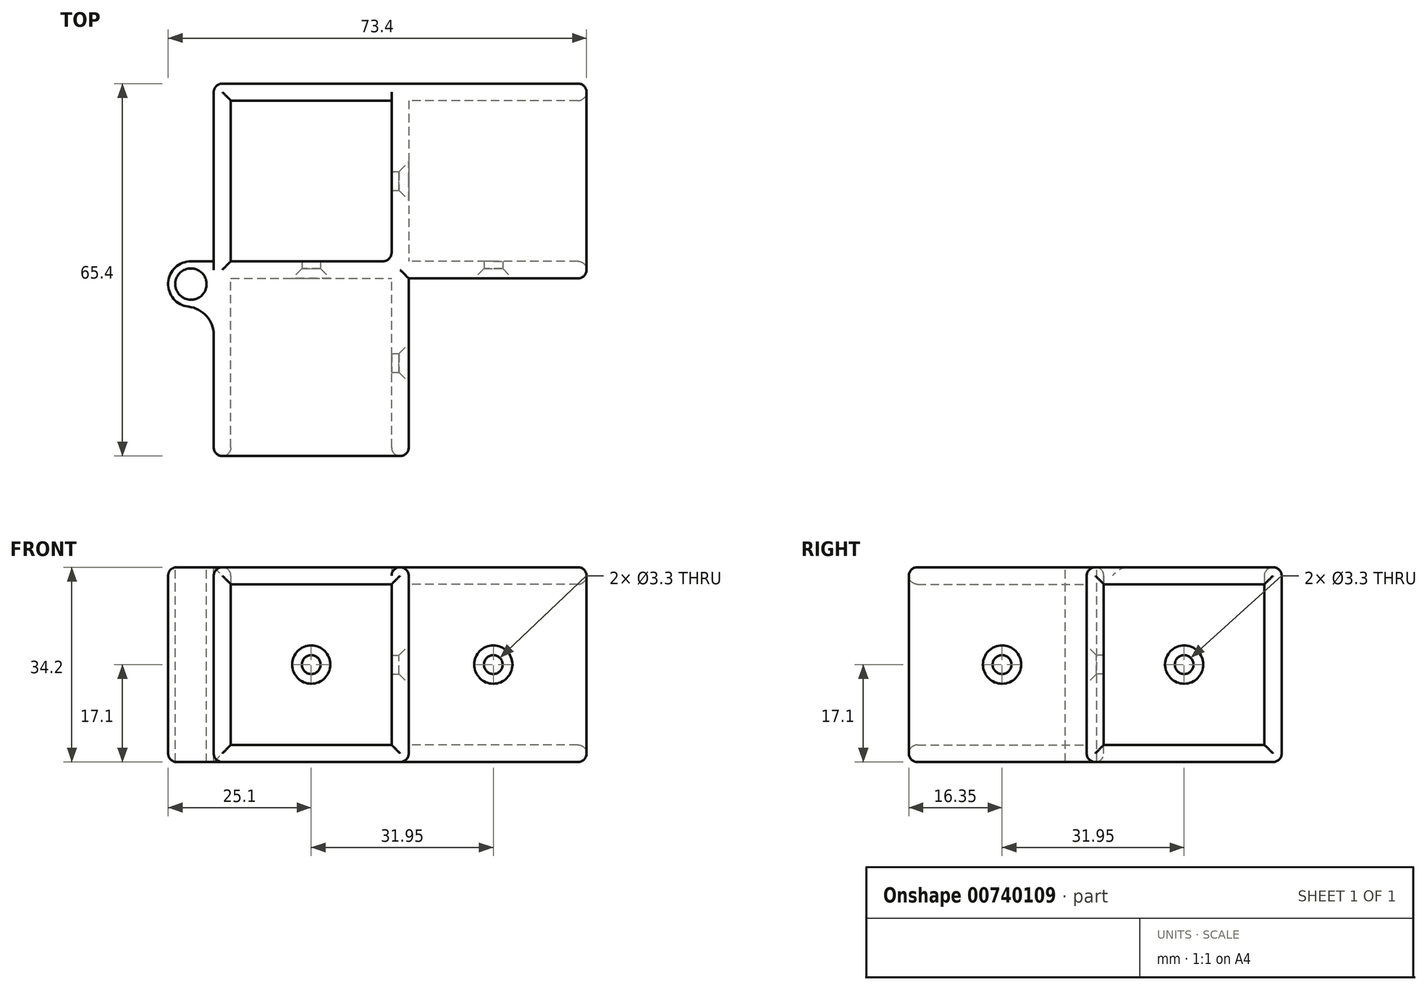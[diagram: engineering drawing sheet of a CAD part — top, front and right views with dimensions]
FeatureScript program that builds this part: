
annotation { "Feature Type Name" : "Feature", "Feature Type Description" : "" }
export const myFeature = defineFeature(function(context is Context, id is Id, definition is map)
    precondition{}
    {
        {
            var Q0;
            Q0=qCreatedBy(makeId("Top.planeOp"),FACE);
            var sketch = newSketch(context, id + "F0", { "sketchPlane" : qUnion([Q0])});
            skLineSegment(sketch, "E0.bottom", {"start": v(0, 0) * mm, "end": v(-28.2, 0) * mm});
            skLineSegment(sketch, "E0.top", {"start": v(0, 28.2) * mm, "end": v(-28.2, 28.2) * mm});
            skLineSegment(sketch, "E0.left", {"start": v(0, 0) * mm, "end": v(0, 28.2) * mm});
            skLineSegment(sketch, "E0.right", {"start": v(-28.2, 0) * mm, "end": v(-28.2, 28.2) * mm});
            skLineSegment(sketch, "E1.0", {"start": v(3, 31.2) * mm, "end": v(-31.2, 31.2) * mm});
            skLineSegment(sketch, "E1.1", {"start": v(3, -3) * mm, "end": v(3, 31.2) * mm});
            skLineSegment(sketch, "E1.2", {"start": v(3, -3) * mm, "end": v(-31.2, -3) * mm});
            skLineSegment(sketch, "E1.3", {"start": v(-31.2, -3) * mm, "end": v(-31.2, 31.2) * mm});
            skPoint(sketch, "E2", {"position": v(-14.1, 14.1) * mm});
            skSolve(sketch);
        }
        {
            var Q0;
            Q0=makeQuery(id+"F0.imprint","IMPRINT",FACE,{"disambiguationData":[TD([[makeQuery(id+"F0.imprint","IMPRINT",EDGE,{"derivedFrom":sQuery(id+"F0.wireOp",EDGE,"E0.bottom")}),1.0]])]});
            var Q1;
            Q1=makeQuery(id+"F0.imprint","IMPRINT",FACE,{"disambiguationData":[TD([[makeQuery(id+"F0.imprint","IMPRINT",EDGE,{"derivedFrom":sQuery(id+"F0.wireOp",EDGE,"E0.bottom")}),-1.0]])]});
            extrude(context, id + "F1", {"entities" : qUnion([Q0, Q1]), "oppositeDirection" : true, "depth" : 3 * mm, "offsetDistance" : 25 * mm});
        }
        {
            var Q0;
            Q0=makeQuery(id+"F0.imprint","IMPRINT",FACE,{"disambiguationData":[TD([[makeQuery(id+"F0.imprint","IMPRINT",EDGE,{"derivedFrom":sQuery(id+"F0.wireOp",EDGE,"E0.bottom")}),1.0]])]});
            extrude(context, id + "F2", {"entities" : qUnion([Q0]), "operationType" : NewBodyOperationType.ADD, "depth" : 31.2 * mm, "offsetDistance" : 25 * mm});
        }
        {
            var Q0;
            {var subQ0=sQuery(id+"F0.wireOp",EDGE,"E1.2");Q0=makeQuery(id+"F2.boolean.opBoolean","MERGE",FACE,{"derivedFrom":[makeQuery(id+"F1.opExtrude","SWEPT_FACE",FACE,{"disambiguationData":[OSD([subQ0])]}),makeQuery(id+"F2.opExtrude","SWEPT_FACE",FACE,{"disambiguationData":[OSD([subQ0])]})]});}
            var sketch = newSketch(context, id + "F3", { "sketchPlane" : qUnion([Q0])});
            skLineSegment(sketch, "E3.bottom", {"start": v(-31.2, 31.2) * mm, "end": v(3, 31.2) * mm});
            skLineSegment(sketch, "E3.top", {"start": v(-31.2, -3) * mm, "end": v(3, -3) * mm});
            skLineSegment(sketch, "E3.left", {"start": v(-31.2, 31.2) * mm, "end": v(-31.2, -3) * mm});
            skLineSegment(sketch, "E3.right", {"start": v(3, 31.2) * mm, "end": v(3, -3) * mm});
            skLineSegment(sketch, "E4.0", {"start": v(-28.2, 28.2) * mm, "end": v(0, 28.2) * mm});
            skLineSegment(sketch, "E4.1", {"start": v(-28.2, 28.2) * mm, "end": v(-28.2, 0) * mm});
            skLineSegment(sketch, "E4.2", {"start": v(-28.2, 0) * mm, "end": v(0, 0) * mm});
            skLineSegment(sketch, "E4.3", {"start": v(0, 28.2) * mm, "end": v(0, 0) * mm});
            skPoint(sketch, "E5", {"position": v(-14.1, 14.1) * mm});
            skSolve(sketch);
        }
        {
            var Q0;
            Q0=makeQuery(id+"F3.imprint","IMPRINT",FACE,{"disambiguationData":[TD([[makeQuery(id+"F3.imprint","IMPRINT",EDGE,{"derivedFrom":sQuery(id+"F3.wireOp",EDGE,"E3.bottom")}),1.0]])]});
            extrude(context, id + "F4", {"entities" : qUnion([Q0]), "operationType" : NewBodyOperationType.ADD, "depth" : 31.2 * mm, "offsetDistance" : 25 * mm});
        }
        {
            var Q0;
            {var subQ0=sQuery(id+"F0.wireOp",EDGE,"E1.1");Q0=makeQuery(id+"F4.boolean.opBoolean","MERGE",FACE,{"derivedFrom":[makeQuery(id+"F2.boolean.opBoolean","MERGE",FACE,{"derivedFrom":[makeQuery(id+"F1.opExtrude","SWEPT_FACE",FACE,{"disambiguationData":[OSD([subQ0])]}),makeQuery(id+"F2.opExtrude","SWEPT_FACE",FACE,{"disambiguationData":[OSD([subQ0])]})]}),makeQuery(id+"F4.opExtrude","SWEPT_FACE",FACE,{"disambiguationData":[OSD([sQuery(id+"F3.wireOp",EDGE,"E3.right")])]})]});}
            var sketch = newSketch(context, id + "F5", { "sketchPlane" : qUnion([Q0])});
            skLineSegment(sketch, "E6.bottom", {"start": v(31.2, 31.2) * mm, "end": v(-3, 31.2) * mm});
            skLineSegment(sketch, "E6.top", {"start": v(31.2, -3) * mm, "end": v(-3, -3) * mm});
            skLineSegment(sketch, "E6.left", {"start": v(31.2, 31.2) * mm, "end": v(31.2, -3) * mm});
            skLineSegment(sketch, "E6.right", {"start": v(-3, 31.2) * mm, "end": v(-3, -3) * mm});
            skLineSegment(sketch, "E7.0", {"start": v(28.2, 28.2) * mm, "end": v(0, 28.2) * mm});
            skLineSegment(sketch, "E7.1", {"start": v(28.2, 28.2) * mm, "end": v(28.2, 0) * mm});
            skLineSegment(sketch, "E7.2", {"start": v(28.2, 0) * mm, "end": v(0, 0) * mm});
            skLineSegment(sketch, "E7.3", {"start": v(0, 28.2) * mm, "end": v(0, 0) * mm});
            skPoint(sketch, "E8", {"position": v(14.1, 14.1) * mm});
            skSolve(sketch);
        }
        {
            var Q0;
            Q0=qSketchRegion(id+"F5",true);
            extrude(context, id + "F6", {"entities" : qUnion([Q0]), "operationType" : NewBodyOperationType.ADD, "depth" : 31.2 * mm, "offsetDistance" : 25 * mm});
        }
        {
            var Q0;
            Q0=sQuery(id+"F5.wireOp",VERTEX,"E8");
            var Q1;
            Q1=sQuery(id+"F3.wireOp",VERTEX,"E5");
            var Q2;
            Q2=makeQuery(id+"F1.opExtrude","SWEPT_BODY",BODY,{"disambiguationData":[OSD([sQuery(id+"F0.wireOp",EDGE,"E1.0"),sQuery(id+"F0.wireOp",EDGE,"E1.1"),sQuery(id+"F0.wireOp",EDGE,"E1.2"),sQuery(id+"F0.wireOp",EDGE,"E1.3")])]});
            hole(context, id + "F7", {"style" : HoleStyle.C_SINK, "endStyle" : HoleEndStyle.BLIND, "standardTappedOrClearance" : lookupTablePath({ "standard" : "ISO", "fit" : "Normal", "size" : "M3", "type" : "Clearance" }), "standardBlindInLast" : lookupTablePath({ "fit" : "Standard", "standard" : "ISO", "size" : "M3", "type" : "Clearance" }), "holeDiameter" : 3.3 * mm, "cSinkDiameter" : 6.72 * mm, "cSinkAngle" : 90 * degree, "majorDiameter" : 5 * mm, "holeDepth" : 13.5 * mm, "isTappedThrough" : true, "tappedDepth" : 12 * mm, "tapClearance" : 3, "startFromSketch" : true, "locations" : qUnion([Q0, Q1]), "scope" : qUnion([Q2])});
        }
        {
            var Q0;
            {var subQ0=sQuery(id+"F3.wireOp",EDGE,"E3.bottom");var subQ3=sQuery(id+"F0.wireOp",EDGE,"E1.1");var subQ5=sQuery(id+"F3.wireOp",EDGE,"E3.right");Q0=makeQuery(id+"F6.boolean.opBoolean","SPLIT",FACE,{"disambiguationData":[TD([makeQuery(id+"F4.opExtrude","SWEPT_FACE",FACE,{"disambiguationData":[OSD([subQ0])]})])],"derivedFrom":makeQuery(id+"F4.boolean.opBoolean","MERGE",FACE,{"derivedFrom":[makeQuery(id+"F2.boolean.opBoolean","MERGE",FACE,{"derivedFrom":[makeQuery(id+"F1.opExtrude","SWEPT_FACE",FACE,{"disambiguationData":[OSD([subQ3])]}),makeQuery(id+"F2.opExtrude","SWEPT_FACE",FACE,{"disambiguationData":[OSD([subQ3])]})]}),makeQuery(id+"F4.opExtrude","SWEPT_FACE",FACE,{"disambiguationData":[OSD([subQ5])]})]})});}
            var sketch = newSketch(context, id + "F8", { "sketchPlane" : qUnion([Q0])});
            skPoint(sketch, "E9", {"position": v(-17.85, 14.1) * mm});
            skSolve(sketch);
        }
        {
            var Q0;
            Q0=makeQuery(id+"F6.opExtrude","SWEPT_FACE",FACE,{"disambiguationData":[OSD([sQuery(id+"F5.wireOp",EDGE,"E6.right")])]});
            var sketch = newSketch(context, id + "F9", { "sketchPlane" : qUnion([Q0])});
            skPoint(sketch, "E10", {"position": v(17.85, 14.1) * mm});
            skSolve(sketch);
        }
        {
            var Q0;
            Q0=sQuery(id+"F9.wireOp",VERTEX,"E10");
            var Q1;
            Q1=sQuery(id+"F8.wireOp",VERTEX,"E9");
            var Q2;
            Q2=makeQuery(id+"F1.opExtrude","SWEPT_BODY",BODY,{"disambiguationData":[OSD([sQuery(id+"F0.wireOp",EDGE,"E1.0"),sQuery(id+"F0.wireOp",EDGE,"E1.1"),sQuery(id+"F0.wireOp",EDGE,"E1.2"),sQuery(id+"F0.wireOp",EDGE,"E1.3")])]});
            hole(context, id + "F10", {"style" : HoleStyle.C_SINK, "endStyle" : HoleEndStyle.BLIND, "standardTappedOrClearance" : lookupTablePath({ "standard" : "ISO", "fit" : "Normal", "size" : "M3", "type" : "Clearance" }), "standardBlindInLast" : lookupTablePath({ "fit" : "Standard", "standard" : "ISO", "size" : "M3", "type" : "Clearance" }), "holeDiameter" : 3.3 * mm, "cSinkDiameter" : 6.72 * mm, "cSinkAngle" : 90 * degree, "majorDiameter" : 5 * mm, "holeDepth" : 13.5 * mm, "isTappedThrough" : true, "tappedDepth" : 12 * mm, "tapClearance" : 3, "startFromSketch" : true, "locations" : qUnion([Q0, Q1]), "scope" : qUnion([Q2])});
        }
        {
            var Q0;
            Q0=makeQuery(id+"F6.boolean.opBoolean","MERGE",FACE,{"derivedFrom":[makeQuery(id+"F4.boolean.opBoolean","MERGE",FACE,{"derivedFrom":[makeQuery(id+"F2.opExtrude","CAP_FACE",FACE,{"disambiguationData":[OSD([sQuery(id+"F0.wireOp",EDGE,"E0.bottom"),sQuery(id+"F0.wireOp",EDGE,"E0.top"),sQuery(id+"F0.wireOp",EDGE,"E0.left"),sQuery(id+"F0.wireOp",EDGE,"E0.right"),sQuery(id+"F0.wireOp",EDGE,"E1.0"),sQuery(id+"F0.wireOp",EDGE,"E1.1"),sQuery(id+"F0.wireOp",EDGE,"E1.2"),sQuery(id+"F0.wireOp",EDGE,"E1.3")])],"isStart":false}),makeQuery(id+"F4.opExtrude","SWEPT_FACE",FACE,{"disambiguationData":[OSD([sQuery(id+"F3.wireOp",EDGE,"E3.bottom")])]})]}),makeQuery(id+"F6.opExtrude","SWEPT_FACE",FACE,{"disambiguationData":[OSD([sQuery(id+"F5.wireOp",EDGE,"E6.bottom")])]})]});
            var sketch = newSketch(context, id + "F11", { "sketchPlane" : qUnion([Q0])});
            skArc(sketch, "E11", {"start": v(-35.2, 0) * mm, "mid": v(-39.2, -4) * mm, "end": v(-35.2, -8) * mm});
            skLineSegment(sketch, "E12", {"start": v(-31.2, 0) * mm, "end": v(-35.2, 0) * mm});
            skLineSegment(sketch, "E13", {"start": v(-31.2, -8) * mm, "end": v(-35.2, -8) * mm});
            skSolve(sketch);
        }
        {
            var Q0;
            Q0=makeQuery(id+"F11.imprint","IMPRINT",FACE,{"disambiguationData":[TD([[makeQuery(id+"F11.imprint","IMPRINT",EDGE,{"derivedFrom":sQuery(id+"F11.wireOp",EDGE,"E11")}),1.0]])]});
            var Q1;
            Q1=makeQuery(id+"F6.boolean.opBoolean","MERGE",FACE,{"derivedFrom":[makeQuery(id+"F4.boolean.opBoolean","MERGE",FACE,{"derivedFrom":[makeQuery(id+"F1.opExtrude","CAP_FACE",FACE,{"disambiguationData":[OSD([sQuery(id+"F0.wireOp",EDGE,"E1.0"),sQuery(id+"F0.wireOp",EDGE,"E1.1"),sQuery(id+"F0.wireOp",EDGE,"E1.2"),sQuery(id+"F0.wireOp",EDGE,"E1.3")])],"isStart":false}),makeQuery(id+"F4.opExtrude","SWEPT_FACE",FACE,{"disambiguationData":[OSD([sQuery(id+"F3.wireOp",EDGE,"E3.top")])]})]}),makeQuery(id+"F6.opExtrude","SWEPT_FACE",FACE,{"disambiguationData":[OSD([sQuery(id+"F5.wireOp",EDGE,"E6.top")])]})]});
            extrude(context, id + "F12", {"entities" : qUnion([Q0]), "operationType" : NewBodyOperationType.ADD, "endBound" : BoundingType.UP_TO_SURFACE, "oppositeDirection" : true, "depth" : 25 * mm, "endBoundEntityFace" : qUnion([Q1]), "offsetDistance" : 25 * mm});
        }
        {
            var Q0;
            Q0=makeQuery(id+"F12.opExtrude","SWEPT_EDGE",EDGE,{"disambiguationData":[OSD([sQuery(id+"F0.wireOp",EDGE,"E1.3"),sQuery(id+"F3.wireOp",EDGE,"E3.bottom"),sQuery(id+"F3.wireOp",EDGE,"E3.left"),sQuery(id+"F11.wireOp",EDGE,"E12")])]});
            var Q1;
            Q1=makeQuery(id+"F12.opExtrude","SWEPT_EDGE",EDGE,{"disambiguationData":[OSD([sQuery(id+"F0.wireOp",EDGE,"E1.3"),sQuery(id+"F3.wireOp",EDGE,"E3.bottom"),sQuery(id+"F3.wireOp",EDGE,"E3.left"),sQuery(id+"F11.wireOp",EDGE,"E13")])]});
            fillet(context, id + "F13", {"entities" : qUnion([Q0, Q1]), "radius" : 5 * mm, "tangentPropagation" : true, "allowEdgeOverflow" : false});
        }
        {
            var Q0;
            {var subQ0=sQuery(id+"F5.wireOp",EDGE,"E6.top");var subQ1=sQuery(id+"F3.wireOp",EDGE,"E3.top");var subQ2=sQuery(id+"F0.wireOp",EDGE,"E1.3");var subQ3=sQuery(id+"F0.wireOp",EDGE,"E1.2");var subQ4=sQuery(id+"F0.wireOp",EDGE,"E1.1");var subQ5=sQuery(id+"F0.wireOp",EDGE,"E1.0");Q0=makeQuery(id+"F13.opFillet","BLEND_EDGE",EDGE,{"blendedFrom":[makeQuery(id+"F12.opExtrude","SWEPT_EDGE",EDGE,{"disambiguationData":[OSD([subQ2,sQuery(id+"F3.wireOp",EDGE,"E3.bottom"),sQuery(id+"F3.wireOp",EDGE,"E3.left"),sQuery(id+"F11.wireOp",EDGE,"E13")])]}),makeQuery(id+"F12.boolean.opBoolean","MERGE",FACE,{"derivedFrom":[makeQuery(id+"F6.boolean.opBoolean","MERGE",FACE,{"derivedFrom":[makeQuery(id+"F4.boolean.opBoolean","MERGE",FACE,{"derivedFrom":[makeQuery(id+"F1.opExtrude","CAP_FACE",FACE,{"disambiguationData":[OSD([subQ5,subQ4,subQ3,subQ2])],"isStart":false}),makeQuery(id+"F4.opExtrude","SWEPT_FACE",FACE,{"disambiguationData":[OSD([subQ1])]})]}),makeQuery(id+"F6.opExtrude","SWEPT_FACE",FACE,{"disambiguationData":[OSD([subQ0])]})]}),makeQuery(id+"F12.opExtrude","CAP_FACE",FACE,{"disambiguationData":[OSD([subQ5,subQ4,subQ3,subQ2,subQ1,subQ0])],"isStart":false})]})],"blendedInto":[makeQuery(id+"F12.boolean.opBoolean","MERGE",FACE,{"derivedFrom":[makeQuery(id+"F6.boolean.opBoolean","MERGE",FACE,{"derivedFrom":[makeQuery(id+"F4.boolean.opBoolean","MERGE",FACE,{"derivedFrom":[makeQuery(id+"F1.opExtrude","CAP_FACE",FACE,{"disambiguationData":[OSD([subQ5,subQ4,subQ3,subQ2])],"isStart":false}),makeQuery(id+"F4.opExtrude","SWEPT_FACE",FACE,{"disambiguationData":[OSD([subQ1])]})]}),makeQuery(id+"F6.opExtrude","SWEPT_FACE",FACE,{"disambiguationData":[OSD([subQ0])]})]}),makeQuery(id+"F12.opExtrude","CAP_FACE",FACE,{"disambiguationData":[OSD([subQ5,subQ4,subQ3,subQ2,subQ1,subQ0])],"isStart":false})]})]});}
            var Q1;
            {var subQ0=sQuery(id+"F11.wireOp",EDGE,"E13");var subQ1=sQuery(id+"F3.wireOp",EDGE,"E3.left");var subQ2=sQuery(id+"F3.wireOp",EDGE,"E3.bottom");var subQ3=sQuery(id+"F0.wireOp",EDGE,"E1.3");Q1=makeQuery(id+"F13.opFillet","BLEND_EDGE",EDGE,{"blendedFrom":[makeQuery(id+"F12.opExtrude","SWEPT_EDGE",EDGE,{"disambiguationData":[OSD([subQ3,subQ2,subQ1,subQ0])]}),makeQuery(id+"F12.boolean.opBoolean","MERGE",FACE,{"derivedFrom":[makeQuery(id+"F6.boolean.opBoolean","MERGE",FACE,{"derivedFrom":[makeQuery(id+"F4.boolean.opBoolean","MERGE",FACE,{"derivedFrom":[makeQuery(id+"F2.opExtrude","CAP_FACE",FACE,{"disambiguationData":[OSD([sQuery(id+"F0.wireOp",EDGE,"E0.bottom"),sQuery(id+"F0.wireOp",EDGE,"E0.top"),sQuery(id+"F0.wireOp",EDGE,"E0.left"),sQuery(id+"F0.wireOp",EDGE,"E0.right"),sQuery(id+"F0.wireOp",EDGE,"E1.0"),sQuery(id+"F0.wireOp",EDGE,"E1.1"),sQuery(id+"F0.wireOp",EDGE,"E1.2"),subQ3])],"isStart":false}),makeQuery(id+"F4.opExtrude","SWEPT_FACE",FACE,{"disambiguationData":[OSD([subQ2])]})]}),makeQuery(id+"F6.opExtrude","SWEPT_FACE",FACE,{"disambiguationData":[OSD([sQuery(id+"F5.wireOp",EDGE,"E6.bottom")])]})]}),makeQuery(id+"F12.opExtrude","CAP_FACE",FACE,{"disambiguationData":[OSD([subQ3,subQ2,subQ1,sQuery(id+"F11.wireOp",EDGE,"E11"),sQuery(id+"F11.wireOp",EDGE,"E12"),subQ0,sQuery(id+"F11.wireOp",EDGE,"fCyymqlx-tuYE-t0qZ-6MRu-04Qh6zcrB8QD")])],"isStart":true})]})],"blendedInto":[makeQuery(id+"F12.boolean.opBoolean","MERGE",FACE,{"derivedFrom":[makeQuery(id+"F6.boolean.opBoolean","MERGE",FACE,{"derivedFrom":[makeQuery(id+"F4.boolean.opBoolean","MERGE",FACE,{"derivedFrom":[makeQuery(id+"F2.opExtrude","CAP_FACE",FACE,{"disambiguationData":[OSD([sQuery(id+"F0.wireOp",EDGE,"E0.bottom"),sQuery(id+"F0.wireOp",EDGE,"E0.top"),sQuery(id+"F0.wireOp",EDGE,"E0.left"),sQuery(id+"F0.wireOp",EDGE,"E0.right"),sQuery(id+"F0.wireOp",EDGE,"E1.0"),sQuery(id+"F0.wireOp",EDGE,"E1.1"),sQuery(id+"F0.wireOp",EDGE,"E1.2"),subQ3])],"isStart":false}),makeQuery(id+"F4.opExtrude","SWEPT_FACE",FACE,{"disambiguationData":[OSD([subQ2])]})]}),makeQuery(id+"F6.opExtrude","SWEPT_FACE",FACE,{"disambiguationData":[OSD([sQuery(id+"F5.wireOp",EDGE,"E6.bottom")])]})]}),makeQuery(id+"F12.opExtrude","CAP_FACE",FACE,{"disambiguationData":[OSD([subQ3,subQ2,subQ1,sQuery(id+"F11.wireOp",EDGE,"E11"),sQuery(id+"F11.wireOp",EDGE,"E12"),subQ0,sQuery(id+"F11.wireOp",EDGE,"fCyymqlx-tuYE-t0qZ-6MRu-04Qh6zcrB8QD")])],"isStart":true})]})]});}
            var Q2;
            Q2=makeQuery(id+"F6.boolean.opBoolean","MERGE",EDGE,{"derivedFrom":[makeQuery(id+"F1.opExtrude","CAP_EDGE",EDGE,{"disambiguationData":[OSD([sQuery(id+"F0.wireOp",EDGE,"E1.0")])],"isStart":false}),makeQuery(id+"F6.opExtrude","SWEPT_EDGE",EDGE,{"disambiguationData":[OSD([sQuery(id+"F5.wireOp",EDGE,"E6.top"),sQuery(id+"F5.wireOp",EDGE,"E6.left")])]})]});
            var Q3;
            Q3=makeQuery(id+"F6.opExtrude","CAP_EDGE",EDGE,{"disambiguationData":[OSD([sQuery(id+"F5.wireOp",EDGE,"E6.left")])],"isStart":false});
            var Q4;
            Q4=makeQuery(id+"F6.boolean.opBoolean","MERGE",EDGE,{"derivedFrom":[makeQuery(id+"F2.opExtrude","CAP_EDGE",EDGE,{"disambiguationData":[OSD([sQuery(id+"F0.wireOp",EDGE,"E1.0")])],"isStart":false}),makeQuery(id+"F6.opExtrude","SWEPT_EDGE",EDGE,{"disambiguationData":[OSD([sQuery(id+"F5.wireOp",EDGE,"E6.bottom"),sQuery(id+"F5.wireOp",EDGE,"E6.left")])]})]});
            var Q5;
            {var subQ0=sQuery(id+"F0.wireOp",EDGE,"E1.3");var subQ1=sQuery(id+"F0.wireOp",EDGE,"E1.0");Q5=makeQuery(id+"F2.boolean.opBoolean","MERGE",EDGE,{"derivedFrom":[makeQuery(id+"F1.opExtrude","SWEPT_EDGE",EDGE,{"disambiguationData":[OSD([subQ1,subQ0])]}),makeQuery(id+"F2.opExtrude","SWEPT_EDGE",EDGE,{"disambiguationData":[OSD([subQ1,subQ0])]})]});}
            var Q6;
            Q6=makeQuery(id+"F4.opExtrude","CAP_EDGE",EDGE,{"disambiguationData":[OSD([sQuery(id+"F3.wireOp",EDGE,"E3.left")])],"isStart":false});
            var Q7;
            Q7=makeQuery(id+"F4.opExtrude","CAP_EDGE",EDGE,{"disambiguationData":[OSD([sQuery(id+"F3.wireOp",EDGE,"E3.top")])],"isStart":false});
            var Q8;
            Q8=makeQuery(id+"F4.opExtrude","CAP_EDGE",EDGE,{"disambiguationData":[OSD([sQuery(id+"F3.wireOp",EDGE,"E3.right")])],"isStart":false});
            var Q9;
            Q9=makeQuery(id+"F4.opExtrude","CAP_EDGE",EDGE,{"disambiguationData":[OSD([sQuery(id+"F3.wireOp",EDGE,"E3.bottom")])],"isStart":false});
            var Q10;
            Q10=makeQuery(id+"F4.opExtrude","CAP_EDGE",EDGE,{"disambiguationData":[OSD([sQuery(id+"F3.wireOp",EDGE,"E4.0")])],"isStart":false});
            var Q11;
            Q11=makeQuery(id+"F4.opExtrude","CAP_EDGE",EDGE,{"disambiguationData":[OSD([sQuery(id+"F3.wireOp",EDGE,"E4.3")])],"isStart":false});
            var Q12;
            Q12=makeQuery(id+"F4.opExtrude","CAP_EDGE",EDGE,{"disambiguationData":[OSD([sQuery(id+"F3.wireOp",EDGE,"E4.2")])],"isStart":false});
            var Q13;
            Q13=makeQuery(id+"F4.opExtrude","CAP_EDGE",EDGE,{"disambiguationData":[OSD([sQuery(id+"F3.wireOp",EDGE,"E4.1")])],"isStart":false});
            var Q14;
            Q14=makeQuery(id+"F4.boolean.opBoolean","MERGE",EDGE,{"derivedFrom":[makeQuery(id+"F1.opExtrude","CAP_EDGE",EDGE,{"disambiguationData":[OSD([sQuery(id+"F0.wireOp",EDGE,"E1.1")])],"isStart":false}),makeQuery(id+"F4.opExtrude","SWEPT_EDGE",EDGE,{"disambiguationData":[OSD([sQuery(id+"F3.wireOp",EDGE,"E3.top"),sQuery(id+"F3.wireOp",EDGE,"E3.right")])]})]});
            var Q15;
            Q15=makeQuery(id+"F6.opExtrude","CAP_EDGE",EDGE,{"disambiguationData":[OSD([sQuery(id+"F5.wireOp",EDGE,"E6.right")])],"isStart":true});
            var Q16;
            Q16=makeQuery(id+"F6.opExtrude","SWEPT_EDGE",EDGE,{"disambiguationData":[OSD([sQuery(id+"F0.wireOp",EDGE,"E1.1"),sQuery(id+"F3.wireOp",EDGE,"E3.top"),sQuery(id+"F3.wireOp",EDGE,"E3.right"),sQuery(id+"F5.wireOp",EDGE,"E6.top"),sQuery(id+"F5.wireOp",EDGE,"E6.right")])]});
            var Q17;
            Q17=makeQuery(id+"F4.boolean.opBoolean","MERGE",EDGE,{"derivedFrom":[makeQuery(id+"F2.opExtrude","CAP_EDGE",EDGE,{"disambiguationData":[OSD([sQuery(id+"F0.wireOp",EDGE,"E1.1")])],"isStart":false}),makeQuery(id+"F4.opExtrude","SWEPT_EDGE",EDGE,{"disambiguationData":[OSD([sQuery(id+"F3.wireOp",EDGE,"E3.bottom"),sQuery(id+"F3.wireOp",EDGE,"E3.right")])]})]});
            var Q18;
            Q18=makeQuery(id+"F6.opExtrude","SWEPT_EDGE",EDGE,{"disambiguationData":[OSD([sQuery(id+"F0.wireOp",EDGE,"E1.1"),sQuery(id+"F3.wireOp",EDGE,"E3.bottom"),sQuery(id+"F3.wireOp",EDGE,"E3.right"),sQuery(id+"F5.wireOp",EDGE,"E6.bottom"),sQuery(id+"F5.wireOp",EDGE,"E6.right")])]});
            var Q19;
            Q19=makeQuery(id+"F6.opExtrude","CAP_EDGE",EDGE,{"disambiguationData":[OSD([sQuery(id+"F5.wireOp",EDGE,"E6.right")])],"isStart":false});
            var Q20;
            Q20=makeQuery(id+"F6.opExtrude","CAP_EDGE",EDGE,{"disambiguationData":[OSD([sQuery(id+"F5.wireOp",EDGE,"E6.top")])],"isStart":false});
            var Q21;
            Q21=makeQuery(id+"F6.opExtrude","CAP_EDGE",EDGE,{"disambiguationData":[OSD([sQuery(id+"F5.wireOp",EDGE,"E7.1")])],"isStart":false});
            var Q22;
            Q22=makeQuery(id+"F6.opExtrude","CAP_EDGE",EDGE,{"disambiguationData":[OSD([sQuery(id+"F5.wireOp",EDGE,"E7.0")])],"isStart":false});
            var Q23;
            Q23=makeQuery(id+"F6.opExtrude","CAP_EDGE",EDGE,{"disambiguationData":[OSD([sQuery(id+"F5.wireOp",EDGE,"E6.bottom")])],"isStart":false});
            var Q24;
            Q24=makeQuery(id+"F6.opExtrude","CAP_EDGE",EDGE,{"disambiguationData":[OSD([sQuery(id+"F5.wireOp",EDGE,"E7.2")])],"isStart":false});
            var Q25;
            Q25=makeQuery(id+"F6.opExtrude","CAP_EDGE",EDGE,{"disambiguationData":[OSD([sQuery(id+"F5.wireOp",EDGE,"E7.3")])],"isStart":false});
            var Q26;
            Q26=makeQuery(id+"F2.opExtrude","CAP_EDGE",EDGE,{"disambiguationData":[OSD([sQuery(id+"F0.wireOp",EDGE,"E0.bottom")])],"isStart":false});
            var Q27;
            Q27=makeQuery(id+"F2.opExtrude","CAP_EDGE",EDGE,{"disambiguationData":[OSD([sQuery(id+"F0.wireOp",EDGE,"E0.right")])],"isStart":false});
            var Q28;
            Q28=makeQuery(id+"F2.opExtrude","CAP_EDGE",EDGE,{"disambiguationData":[OSD([sQuery(id+"F0.wireOp",EDGE,"E0.top")])],"isStart":false});
            var Q29;
            Q29=makeQuery(id+"F2.opExtrude","SWEPT_EDGE",EDGE,{"disambiguationData":[OSD([sQuery(id+"F0.wireOp",EDGE,"E0.bottom"),sQuery(id+"F0.wireOp",EDGE,"E0.left")])]});
            fillet(context, id + "F14", {"entities" : qUnion([Q0, Q1, Q2, Q3, Q4, Q5, Q6, Q7, Q8, Q9, Q10, Q11, Q12, Q13, Q14, Q15, Q16, Q17, Q18, Q19, Q20, Q21, Q22, Q23, Q24, Q25, Q26, Q27, Q28, Q29]), "radius" : 1.5 * mm, "tangentPropagation" : true, "allowEdgeOverflow" : false});
        }
        {
            var Q0;
            Q0=sQuery(id+"F11.wireOp",VERTEX,"E11.center");
            var Q1;
            Q1=makeQuery(id+"F1.opExtrude","SWEPT_BODY",BODY,{"disambiguationData":[OSD([sQuery(id+"F0.wireOp",EDGE,"E1.0"),sQuery(id+"F0.wireOp",EDGE,"E1.1"),sQuery(id+"F0.wireOp",EDGE,"E1.2"),sQuery(id+"F0.wireOp",EDGE,"E1.3")])]});
            hole(context, id + "F15", {"style" : HoleStyle.SIMPLE, "endStyle" : HoleEndStyle.THROUGH, "standardTappedOrClearance" : lookupTablePath({ "standard" : "ISO", "fit" : "Normal", "size" : "M5", "type" : "Clearance" }), "standardBlindInLast" : lookupTablePath({ "fit" : "Standard", "standard" : "ISO", "size" : "M5", "type" : "Clearance" }), "holeDiameter" : 5.5 * mm, "majorDiameter" : 5 * mm, "isTappedThrough" : true, "tappedDepth" : 12 * mm, "tapClearance" : 3, "startFromSketch" : true, "locations" : qUnion([Q0]), "scope" : qUnion([Q1])});
        }
    });
